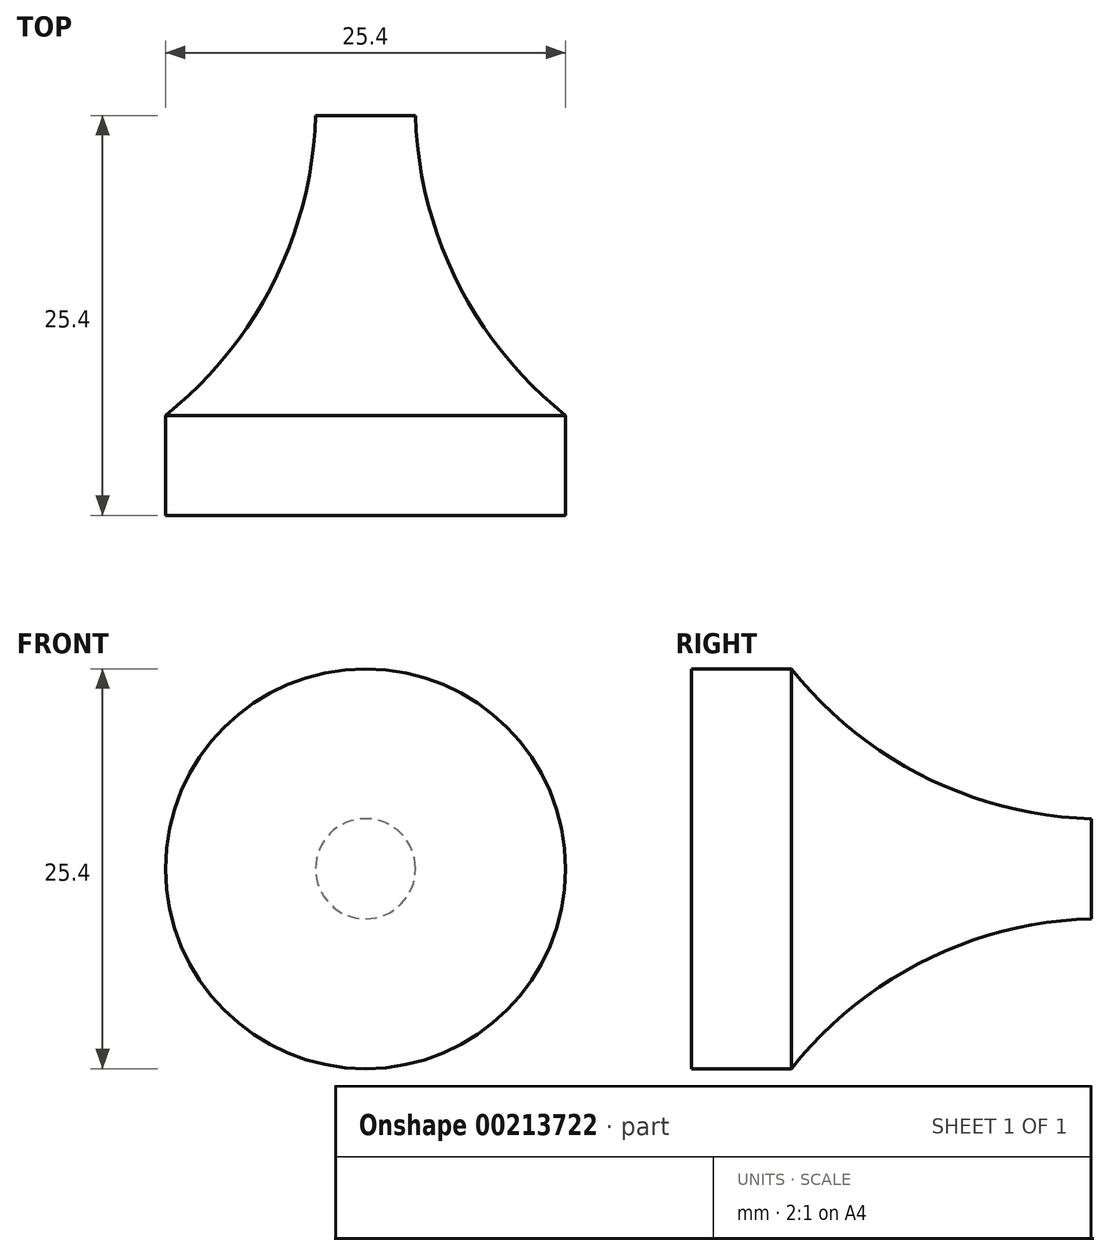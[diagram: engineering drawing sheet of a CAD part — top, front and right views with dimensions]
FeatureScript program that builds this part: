
annotation { "Feature Type Name" : "Feature", "Feature Type Description" : "" }
export const myFeature = defineFeature(function(context is Context, id is Id, definition is map)
    precondition{}
    {
        {
            var Q0;
            Q0=qCreatedBy(makeId("Top.planeOp"),FACE);
            var sketch = newSketch(context, id + "F0", { "sketchPlane" : qUnion([Q0])});
            skLineSegment(sketch, "E0", {"start": v(0, 10.42) * mm, "end": v(0, -14.98) * mm});
            skLineSegment(sketch, "E1", {"start": v(0, -14.98) * mm, "end": v(-12.7, -14.98) * mm});
            skLineSegment(sketch, "E2", {"start": v(-12.7, -14.98) * mm, "end": v(-12.7, -8.63) * mm});
            skArc(sketch, "E3", {"start": v(-12.7, -8.63) * mm, "mid": v(-5.83, -0.16) * mm, "end": v(-3.17, 10.42) * mm});
            skLineSegment(sketch, "E4", {"start": v(-3.18, 10.42) * mm, "end": v(0, 10.42) * mm});
            skSolve(sketch);
        }
        {
            var Q0;
            Q0=makeQuery(id+"F0.imprint","IMPRINT",FACE,{"disambiguationData":[TD([[makeQuery(id+"F0.imprint","IMPRINT",EDGE,{"derivedFrom":sQuery(id+"F0.wireOp",EDGE,"E0")}),-1.0]])]});
            var Q1;
            Q1=sQuery(id+"F0.wireOp",EDGE,"E0");
            revolve(context, id + "F1", {"entities" : qUnion([Q0]), "axis" : qUnion([Q1]), "revolveType" : RevolveType.FULL});
        }
    });
